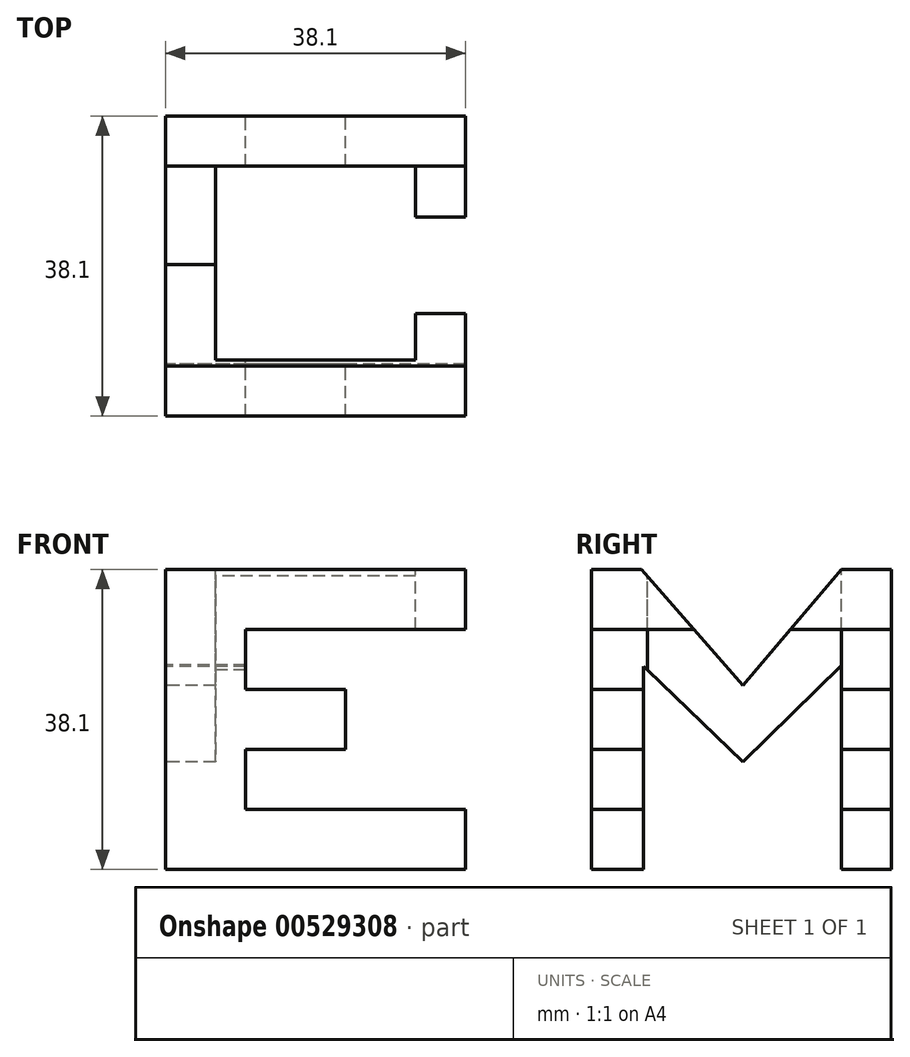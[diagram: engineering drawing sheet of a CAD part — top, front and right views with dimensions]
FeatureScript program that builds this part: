
annotation { "Feature Type Name" : "Feature", "Feature Type Description" : "" }
export const myFeature = defineFeature(function(context is Context, id is Id, definition is map)
    precondition{}
    {
        {
            var Q0;
            Q0=qCreatedBy(makeId("Front.planeOp"),FACE);
            var sketch = newSketch(context, id + "F0", { "sketchPlane" : qUnion([Q0])});
            skLineSegment(sketch, "E0.bottom", {"start": v(0, 0) * mm, "end": v(38.1, 0) * mm});
            skLineSegment(sketch, "E0.top", {"start": v(0, 38.1) * mm, "end": v(38.1, 38.1) * mm});
            skLineSegment(sketch, "E0.left", {"start": v(0, 0) * mm, "end": v(0, 38.1) * mm});
            skLineSegment(sketch, "E0.right", {"start": v(38.1, 0) * mm, "end": v(38.1, 38.1) * mm});
            skSolve(sketch);
        }
        {
            var Q0;
            Q0=qCreatedBy(makeId("Front.planeOp"),FACE);
            var sketch = newSketch(context, id + "F1", { "sketchPlane" : qUnion([Q0])});
            skSolve(sketch);
        }
        {
            var Q0;
            Q0=qSketchRegion(id+"F1",true);
            var Q1;
            Q1=makeQuery(id+"F0.imprint","IMPRINT",FACE,{"disambiguationData":[TD([[makeQuery(id+"F0.imprint","IMPRINT",EDGE,{"derivedFrom":sQuery(id+"F0.wireOp",EDGE,"E0.bottom")}),1.0]])]});
            extrude(context, id + "F2", {"entities" : qUnion([Q0, Q1]), "depth" : 38.1 * mm});
        }
        {
            var Q0;
            Q0=qCreatedBy(makeId("Front.planeOp"),FACE);
            var sketch = newSketch(context, id + "F3", { "sketchPlane" : qUnion([Q0])});
            skLineSegment(sketch, "E1", {"start": v(0, 0) * mm, "end": v(0, 38.1) * mm});
            skLineSegment(sketch, "E2", {"start": v(0, 38.1) * mm, "end": v(38.1, 38.1) * mm});
            skLineSegment(sketch, "E3", {"start": v(38.1, 38.1) * mm, "end": v(38.1, 30.48) * mm});
            skLineSegment(sketch, "E4", {"start": v(38.1, 30.48) * mm, "end": v(10.16, 30.48) * mm});
            skLineSegment(sketch, "E5", {"start": v(10.16, 30.48) * mm, "end": v(10.16, 22.86) * mm});
            skLineSegment(sketch, "E6", {"start": v(10.16, 22.86) * mm, "end": v(22.86, 22.86) * mm});
            skLineSegment(sketch, "E7", {"start": v(22.86, 22.86) * mm, "end": v(22.86, 15.24) * mm});
            skLineSegment(sketch, "E8", {"start": v(22.86, 15.24) * mm, "end": v(10.16, 15.24) * mm});
            skLineSegment(sketch, "E9", {"start": v(10.16, 15.24) * mm, "end": v(10.16, 7.62) * mm});
            skLineSegment(sketch, "E10", {"start": v(10.16, 7.62) * mm, "end": v(38.1, 7.62) * mm});
            skLineSegment(sketch, "E11", {"start": v(38.1, 7.62) * mm, "end": v(38.1, 0) * mm});
            skLineSegment(sketch, "E12", {"start": v(38.1, 7.62) * mm, "end": v(38.1, 30.48) * mm});
            skSolve(sketch);
        }
        {
            var Q0;
            Q0=makeQuery(id+"F3.imprint","IMPRINT",FACE,{"disambiguationData":[TD([[makeQuery(id+"F3.imprint","IMPRINT",EDGE,{"derivedFrom":sQuery(id+"F3.wireOp",EDGE,"E4")}),1.0]])]});
            extrude(context, id + "F4", {"entities" : qUnion([Q0]), "operationType" : NewBodyOperationType.REMOVE, "depth" : 38.1 * mm});
        }
        {
            var Q0;
            Q0=qCreatedBy(makeId("Top.planeOp"),FACE);
            cPlane(context, id + "F5", {"entities" : qUnion([Q0]), "cplaneType" : CPlaneType.OFFSET, "offset" : 38.1 * mm, "width" : 152.4 * mm, "height" : 152.4 * mm});
        }
        {
            var Q0;
            Q0=qCreatedBy(id+"F5.planeOp",FACE);
            var sketch = newSketch(context, id + "F6", { "sketchPlane" : qUnion([Q0])});
            skLineSegment(sketch, "E13", {"start": v(0, 0) * mm, "end": v(0, -38.1) * mm});
            skLineSegment(sketch, "E14", {"start": v(0, -38.1) * mm, "end": v(38.1, -38.1) * mm});
            skLineSegment(sketch, "E15", {"start": v(38.1, -38.1) * mm, "end": v(38.1, 0) * mm});
            skLineSegment(sketch, "E16", {"start": v(0, 0) * mm, "end": v(38.1, 0) * mm});
            skLineSegment(sketch, "E17", {"start": v(6.35, -6.38) * mm, "end": v(31.75, -6.38) * mm});
            skLineSegment(sketch, "E18", {"start": v(31.75, -6.38) * mm, "end": v(31.75, -31.02) * mm});
            skLineSegment(sketch, "E19", {"start": v(31.75, -31.02) * mm, "end": v(6.35, -31.02) * mm});
            skLineSegment(sketch, "E20", {"start": v(6.35, -31.02) * mm, "end": v(6.35, -6.38) * mm});
            skSolve(sketch);
        }
        {
            var Q0;
            Q0=qCreatedBy(id+"F5.planeOp",FACE);
            var sketch = newSketch(context, id + "F7", { "sketchPlane" : qUnion([Q0])});
            skSolve(sketch);
        }
        {
            var Q0;
            Q0=qSketchRegion(id+"F7",true);
            var Q1;
            Q1=makeQuery(id+"F6.imprint","IMPRINT",FACE,{"disambiguationData":[TD([[makeQuery(id+"F6.imprint","IMPRINT",EDGE,{"derivedFrom":sQuery(id+"F6.wireOp",EDGE,"E17")}),-1.0]])]});
            extrude(context, id + "F8", {"entities" : qUnion([Q0, Q1]), "operationType" : NewBodyOperationType.REMOVE, "oppositeDirection" : true, "depth" : 38.1 * mm});
        }
        {
            var Q0;
            Q0=qCreatedBy(makeId("Right.planeOp"),FACE);
            var sketch = newSketch(context, id + "F9", { "sketchPlane" : qUnion([Q0])});
            skLineSegment(sketch, "E21", {"start": v(0, 0) * mm, "end": v(-6.35, 0) * mm});
            skLineSegment(sketch, "E22", {"start": v(-6.35, 0) * mm, "end": v(-6.35, 21.6) * mm});
            skLineSegment(sketch, "E23", {"start": v(-6.35, 21.6) * mm, "end": v(-18.86, 10.86) * mm});
            skLineSegment(sketch, "E24", {"start": v(-18.86, 10.86) * mm, "end": v(-31.78, 21.63) * mm});
            skLineSegment(sketch, "E25", {"start": v(-31.78, 21.63) * mm, "end": v(-31.78, 0) * mm});
            skLineSegment(sketch, "E26", {"start": v(-6.35, 38.1) * mm, "end": v(-18.86, 23.38) * mm});
            skLineSegment(sketch, "E27", {"start": v(-18.86, 23.38) * mm, "end": v(-31.78, 38.15) * mm});
            skLineSegment(sketch, "E28", {"start": v(-6.35, 38.1) * mm, "end": v(0, 38.1) * mm});
            skLineSegment(sketch, "E29", {"start": v(0, 38.1) * mm, "end": v(0, 0) * mm});
            skLineSegment(sketch, "E30", {"start": v(-38.13, 0) * mm, "end": v(-38.13, 38.1) * mm});
            skLineSegment(sketch, "E31", {"start": v(-38.13, 38.1) * mm, "end": v(-6.35, 38.1) * mm});
            skLineSegment(sketch, "E32", {"start": v(-38.13, 38.1) * mm, "end": v(-31.78, 38.15) * mm});
            skLineSegment(sketch, "E33", {"start": v(-31.78, 0) * mm, "end": v(-38.13, 0) * mm});
            skLineSegment(sketch, "E34", {"start": v(0, 38.1) * mm, "end": v(-38.13, 38.1) * mm});
            skLineSegment(sketch, "E35", {"start": v(-6.35, 0) * mm, "end": v(-31.78, 0) * mm});
            skSolve(sketch);
        }
        {
            var Q0;
            {var subQ0=sQuery(id+"F9.wireOp",EDGE,"E26");Q0=makeQuery(id+"F9.imprint","IMPRINT",FACE,{"disambiguationData":[TD([[makeQuery(id+"F9.imprint","IMPRINT",EDGE,{"derivedFrom":subQ0}),-1.0]])]});}
            extrude(context, id + "F10", {"entities" : qUnion([Q0]), "operationType" : NewBodyOperationType.REMOVE, "depth" : 38.1 * mm});
        }
        {
            var Q0;
            Q0=qCreatedBy(makeId("Right.planeOp"),FACE);
            var sketch = newSketch(context, id + "F11", { "sketchPlane" : qUnion([Q0])});
            skLineSegment(sketch, "E36", {"start": v(-6.35, 0) * mm, "end": v(-6.35, 25.96) * mm});
            skLineSegment(sketch, "E37", {"start": v(-6.35, 25.96) * mm, "end": v(-18.89, 13.65) * mm});
            skLineSegment(sketch, "E38", {"start": v(-18.89, 13.65) * mm, "end": v(-31.5, 25.79) * mm});
            skLineSegment(sketch, "E39", {"start": v(-31.5, 25.79) * mm, "end": v(-31.5, 0) * mm});
            skLineSegment(sketch, "E40", {"start": v(-6.35, 0) * mm, "end": v(0, 0) * mm});
            skLineSegment(sketch, "E41", {"start": v(-6.35, 0) * mm, "end": v(-31.5, 0) * mm});
            skLineSegment(sketch, "E42", {"start": v(0, 0) * mm, "end": v(-6.35, 0) * mm});
            skLineSegment(sketch, "E43", {"start": v(-31.5, 0) * mm, "end": v(-37.85, 0) * mm});
            skLineSegment(sketch, "E44", {"start": v(-37.85, 0) * mm, "end": v(-37.85, 38.1) * mm});
            skSolve(sketch);
        }
        {
            var Q0;
            Q0=qSketchRegion(id+"F11",true);
            extrude(context, id + "F12", {"entities" : qUnion([Q0]), "operationType" : NewBodyOperationType.REMOVE, "depth" : 38.1 * mm});
        }
    });
